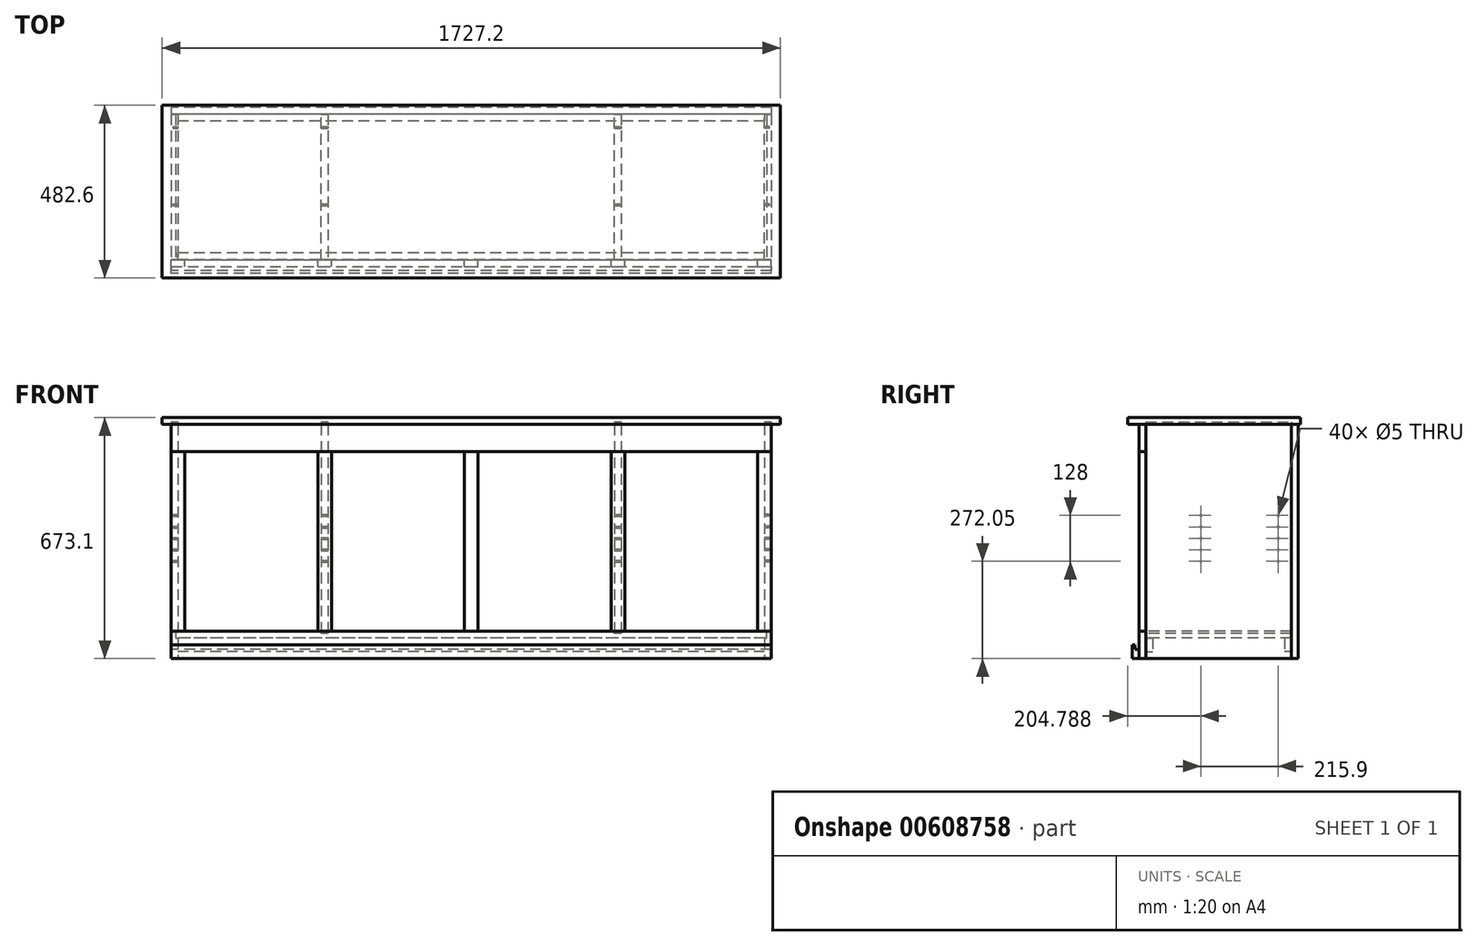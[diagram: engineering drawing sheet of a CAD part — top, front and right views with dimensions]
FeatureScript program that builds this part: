
annotation { "Feature Type Name" : "Feature", "Feature Type Description" : "" }
export const myFeature = defineFeature(function(context is Context, id is Id, definition is map)
    precondition{}
    {
        {
            var Q0;
            Q0=qCreatedBy(makeId("Front.planeOp"),FACE);
            var sketch = newSketch(context, id + "F0", { "sketchPlane" : qUnion([Q0])});
            skLineSegment(sketch, "E0.bottom", {"start": v(838.2, -336.55) * mm, "end": v(-838.2, -336.55) * mm});
            skLineSegment(sketch, "E0.top", {"start": v(838.2, 336.55) * mm, "end": v(-838.2, 336.55) * mm});
            skLineSegment(sketch, "E0.left", {"start": v(838.2, -336.55) * mm, "end": v(838.2, 336.55) * mm});
            skLineSegment(sketch, "E0.right", {"start": v(-838.2, -336.55) * mm, "end": v(-838.2, 336.55) * mm});
            skPoint(sketch, "E0.middle", {"position": v(0, 0) * mm});
            skLineSegment(sketch, "E1", {"start": v(-838.2, 317.5) * mm, "end": v(838.2, 317.5) * mm});
            skLineSegment(sketch, "E2", {"start": v(-838.2, -298.45) * mm, "end": v(838.2, -298.45) * mm});
            skLineSegment(sketch, "E3", {"start": v(-838.2, -260.35) * mm, "end": v(838.2, -260.35) * mm});
            skLineSegment(sketch, "E4", {"start": v(-838.2, 241.3) * mm, "end": v(838.2, 241.3) * mm});
            skLineSegment(sketch, "E5", {"start": v(-800.1, 241.3) * mm, "end": v(-800.1, -260.35) * mm});
            skLineSegment(sketch, "E6", {"start": v(800.1, 241.3) * mm, "end": v(800.1, -260.35) * mm});
            skLineSegment(sketch, "E7", {"start": v(-428.63, 241.3) * mm, "end": v(-428.62, -260.35) * mm});
            skLineSegment(sketch, "E8", {"start": v(-390.53, 241.3) * mm, "end": v(-390.52, -260.35) * mm});
            skLineSegment(sketch, "E9", {"start": v(428.63, 241.3) * mm, "end": v(428.63, -260.35) * mm});
            skLineSegment(sketch, "E10", {"start": v(390.53, 241.3) * mm, "end": v(390.53, -260.35) * mm});
            skLineSegment(sketch, "E11", {"start": v(-19.05, 241.3) * mm, "end": v(-19.05, -260.35) * mm});
            skLineSegment(sketch, "E12", {"start": v(19.05, 241.3) * mm, "end": v(19.05, -260.35) * mm});
            skLineSegment(sketch, "E13", {"start": v(-800.1, -9.53) * mm, "end": v(-428.62, -9.53) * mm, "construction": true});
            skLineSegment(sketch, "E14", {"start": v(-390.52, -9.53) * mm, "end": v(-19.05, -9.52) * mm, "construction": true});
            skLineSegment(sketch, "E15", {"start": v(19.05, -9.52) * mm, "end": v(390.53, -9.52) * mm, "construction": true});
            skLineSegment(sketch, "E16", {"start": v(428.63, -9.52) * mm, "end": v(800.1, -9.52) * mm, "construction": true});
            skLineSegment(sketch, "E17", {"start": v(819.15, 317.5) * mm, "end": v(819.15, -336.55) * mm});
            skLineSegment(sketch, "E18", {"start": v(-819.15, 317.5) * mm, "end": v(-819.15, -336.55) * mm});
            skLineSegment(sketch, "E19", {"start": v(-838.2, -279.4) * mm, "end": v(838.2, -279.4) * mm});
            skLineSegment(sketch, "E20", {"start": v(-419.1, 317.5) * mm, "end": v(-419.1, -260.35) * mm});
            skLineSegment(sketch, "E21", {"start": v(-400.05, 317.5) * mm, "end": v(-400.05, -260.35) * mm});
            skLineSegment(sketch, "E22", {"start": v(400.05, 317.5) * mm, "end": v(400.05, -260.35) * mm});
            skLineSegment(sketch, "E23", {"start": v(419.1, 317.5) * mm, "end": v(419.1, -260.35) * mm});
            skLineSegment(sketch, "E24", {"start": v(-400.05, -260.35) * mm, "end": v(-400.05, -266.7) * mm});
            skLineSegment(sketch, "E25", {"start": v(-400.05, -266.7) * mm, "end": v(-419.1, -266.7) * mm});
            skLineSegment(sketch, "E26", {"start": v(-419.1, -266.7) * mm, "end": v(-419.1, -260.35) * mm});
            skLineSegment(sketch, "E27", {"start": v(400.05, -260.35) * mm, "end": v(400.05, -266.7) * mm});
            skLineSegment(sketch, "E28", {"start": v(419.1, -260.35) * mm, "end": v(419.1, -266.7) * mm});
            skLineSegment(sketch, "E29", {"start": v(419.1, -266.7) * mm, "end": v(400.05, -266.7) * mm});
            skLineSegment(sketch, "E30", {"start": v(825.5, -260.35) * mm, "end": v(825.5, -279.4) * mm});
            skLineSegment(sketch, "E31", {"start": v(-825.5, -260.35) * mm, "end": v(-825.5, -279.4) * mm});
            skLineSegment(sketch, "E32", {"start": v(-838.2, 336.55) * mm, "end": v(-863.6, 336.55) * mm});
            skLineSegment(sketch, "E33", {"start": v(-838.2, 317.5) * mm, "end": v(-863.6, 317.5) * mm});
            skLineSegment(sketch, "E34", {"start": v(-863.6, 336.55) * mm, "end": v(-863.6, 317.5) * mm});
            skLineSegment(sketch, "E35", {"start": v(838.2, 336.55) * mm, "end": v(863.6, 336.55) * mm});
            skLineSegment(sketch, "E36", {"start": v(838.2, 317.5) * mm, "end": v(863.6, 317.5) * mm});
            skLineSegment(sketch, "E37", {"start": v(863.6, 317.5) * mm, "end": v(863.6, 336.55) * mm});
            skLineSegment(sketch, "E38", {"start": v(819.15, 317.5) * mm, "end": v(819.15, 323.85) * mm});
            skLineSegment(sketch, "E39", {"start": v(819.15, 323.85) * mm, "end": v(838.2, 323.85) * mm});
            skLineSegment(sketch, "E40", {"start": v(400.05, 317.5) * mm, "end": v(400.05, 323.85) * mm});
            skLineSegment(sketch, "E41", {"start": v(400.05, 323.85) * mm, "end": v(419.1, 323.85) * mm});
            skLineSegment(sketch, "E42", {"start": v(419.1, 323.85) * mm, "end": v(419.1, 317.5) * mm});
            skLineSegment(sketch, "E43", {"start": v(-419.1, 317.5) * mm, "end": v(-419.1, 323.85) * mm});
            skLineSegment(sketch, "E44", {"start": v(-419.1, 323.85) * mm, "end": v(-400.05, 323.85) * mm});
            skLineSegment(sketch, "E45", {"start": v(-400.05, 323.85) * mm, "end": v(-400.05, 317.5) * mm});
            skLineSegment(sketch, "E46", {"start": v(-819.15, 317.5) * mm, "end": v(-819.15, 323.85) * mm});
            skLineSegment(sketch, "E47", {"start": v(-819.15, 323.85) * mm, "end": v(-838.2, 323.85) * mm});
            skSolve(sketch);
        }
        {
            var Q0;
            Q0=qCreatedBy(makeId("Right.planeOp"),FACE);
            var sketch = newSketch(context, id + "F1", { "sketchPlane" : qUnion([Q0])});
            skSolve(sketch);
        }
        {
            var Q0;
            Q0 = qSketchRegion(id + "F1", true);
            var Q1;
            {var subQ4=sQuery(id+"F0.wireOp",EDGE,"E1");Q1=makeQuery(id+"F0.imprint","IMPRINT",FACE,{"disambiguationData":[TD([[makeQuery(id+"F0.imprint","IMPRINT",EDGE,{"derivedFrom":subQ4}),-1.0]])]});}
            var Q2;
            {var subQ2=sQuery(id+"F0.wireOp",EDGE,"E17");var subQ6=sQuery(id+"F0.wireOp",EDGE,"E1");var subQ7=makeQuery(id+"F0.imprint","INTERSECT",VERTEX,{"derivedFrom":[subQ6,subQ2]});Q2=makeQuery(id+"F0.imprint","IMPRINT",FACE,{"disambiguationData":[TD([[makeQuery(id+"F0.imprint","IMPRINT",EDGE,{"disambiguationData":[TD([[subQ7,1.0]])],"derivedFrom":subQ6}),-1.0]])]});}
            var Q3;
            {var subQ4=sQuery(id+"F0.wireOp",EDGE,"E1");var subQ7=sQuery(id+"F0.wireOp",EDGE,"E18");var subQ9=makeQuery(id+"F0.imprint","INTERSECT",VERTEX,{"derivedFrom":[subQ4,subQ7]});Q3=makeQuery(id+"F0.imprint","IMPRINT",FACE,{"disambiguationData":[TD([[makeQuery(id+"F0.imprint","IMPRINT",EDGE,{"disambiguationData":[TD([[subQ9,-1.0]])],"derivedFrom":subQ4}),-1.0]])]});}
            var Q4;
            {var subQ4=sQuery(id+"F0.wireOp",EDGE,"E1");var subQ8=sQuery(id+"F0.wireOp",EDGE,"E21");var subQ10=makeQuery(id+"F0.imprint","INTERSECT",VERTEX,{"derivedFrom":[subQ4,subQ8]});Q4=makeQuery(id+"F0.imprint","IMPRINT",FACE,{"disambiguationData":[TD([[makeQuery(id+"F0.imprint","IMPRINT",EDGE,{"disambiguationData":[TD([[subQ10,-1.0]])],"derivedFrom":subQ4}),-1.0]])]});}
            extrude(context, id + "F2", {"entities" : qUnion([Q0, Q1, Q2, Q3, Q4]), "depth" : 19.05 * mm, "offsetDistance" : 25.4 * mm});
        }
        {
            var Q0;
            {var subQ0=sQuery(id+"F0.wireOp",EDGE,"E18");var subQ1=sQuery(id+"F0.wireOp",EDGE,"E2");var subQ2=makeQuery(id+"F0.imprint","INTERSECT",VERTEX,{"derivedFrom":[subQ1,subQ0]});Q0=makeQuery(id+"F0.imprint","IMPRINT",FACE,{"disambiguationData":[TD([[makeQuery(id+"F0.imprint","IMPRINT",EDGE,{"disambiguationData":[TD([[subQ2,-1.0]])],"derivedFrom":subQ1}),1.0]])]});}
            var Q1;
            {var subQ0=sQuery(id+"F0.wireOp",EDGE,"E0.left");var subQ1=sQuery(id+"F0.wireOp",EDGE,"E0.bottom");var subQ2=makeQuery(id+"F0.imprint","INTERSECT",VERTEX,{"derivedFrom":[subQ1,subQ0]});Q1=makeQuery(id+"F0.imprint","IMPRINT",FACE,{"disambiguationData":[TD([[makeQuery(id+"F0.imprint","IMPRINT",EDGE,{"disambiguationData":[TD([[subQ2,-1.0]])],"derivedFrom":subQ1}),-1.0]])]});}
            var Q2;
            {var subQ0=sQuery(id+"F0.wireOp",EDGE,"E0.right");var subQ1=sQuery(id+"F0.wireOp",EDGE,"E0.bottom");var subQ2=makeQuery(id+"F0.imprint","INTERSECT",VERTEX,{"derivedFrom":[subQ1,subQ0]});Q2=makeQuery(id+"F0.imprint","IMPRINT",FACE,{"disambiguationData":[TD([[makeQuery(id+"F0.imprint","IMPRINT",EDGE,{"disambiguationData":[TD([[subQ2,1.0]])],"derivedFrom":subQ1}),-1.0]])]});}
            var Q3;
            {var subQ0=sQuery(id+"F0.wireOp",EDGE,"E17");var subQ1=sQuery(id+"F0.wireOp",EDGE,"E0.bottom");var subQ2=makeQuery(id+"F0.imprint","INTERSECT",VERTEX,{"derivedFrom":[subQ1,subQ0]});Q3=makeQuery(id+"F0.imprint","IMPRINT",FACE,{"disambiguationData":[TD([[makeQuery(id+"F0.imprint","IMPRINT",EDGE,{"disambiguationData":[TD([[subQ2,-1.0]])],"derivedFrom":subQ1}),-1.0]])]});}
            var Q4;
            {var subQ5=sQuery(id+"F0.wireOp",EDGE,"E31");Q4=makeQuery(id+"F0.imprint","IMPRINT",FACE,{"disambiguationData":[TD([[makeQuery(id+"F0.imprint","IMPRINT",EDGE,{"derivedFrom":subQ5}),-1.0]])]});}
            var Q5;
            {var subQ14=sQuery(id+"F0.wireOp",EDGE,"E24");Q5=makeQuery(id+"F0.imprint","IMPRINT",FACE,{"disambiguationData":[TD([[makeQuery(id+"F0.imprint","IMPRINT",EDGE,{"derivedFrom":subQ14}),1.0]])]});}
            var Q6;
            {var subQ5=sQuery(id+"F0.wireOp",EDGE,"E30");Q6=makeQuery(id+"F0.imprint","IMPRINT",FACE,{"disambiguationData":[TD([[makeQuery(id+"F0.imprint","IMPRINT",EDGE,{"derivedFrom":subQ5}),1.0]])]});}
            var Q7;
            {var subQ0=sQuery(id+"F0.wireOp",EDGE,"E31");Q7=makeQuery(id+"F0.imprint","IMPRINT",FACE,{"disambiguationData":[TD([[makeQuery(id+"F0.imprint","IMPRINT",EDGE,{"derivedFrom":subQ0}),1.0]])]});}
            var Q8;
            {var subQ1=sQuery(id+"F0.wireOp",EDGE,"E2");var subQ5=sQuery(id+"F0.wireOp",EDGE,"E0.right");var subQ6=makeQuery(id+"F0.imprint","INTERSECT",VERTEX,{"derivedFrom":[subQ5,subQ1]});Q8=makeQuery(id+"F0.imprint","IMPRINT",FACE,{"disambiguationData":[TD([[makeQuery(id+"F0.imprint","IMPRINT",EDGE,{"disambiguationData":[TD([[subQ6,-1.0]])],"derivedFrom":subQ5}),-1.0]])]});}
            var Q9;
            {var subQ2=sQuery(id+"F0.wireOp",EDGE,"E24");Q9=makeQuery(id+"F0.imprint","IMPRINT",FACE,{"disambiguationData":[TD([[makeQuery(id+"F0.imprint","IMPRINT",EDGE,{"derivedFrom":subQ2}),-1.0]])]});}
            var Q10;
            {var subQ0=sQuery(id+"F0.wireOp",EDGE,"E27");Q10=makeQuery(id+"F0.imprint","IMPRINT",FACE,{"disambiguationData":[TD([[makeQuery(id+"F0.imprint","IMPRINT",EDGE,{"derivedFrom":subQ0}),1.0]])]});}
            var Q11;
            {var subQ4=sQuery(id+"F0.wireOp",EDGE,"E2");var subQ6=sQuery(id+"F0.wireOp",EDGE,"E0.left");var subQ7=makeQuery(id+"F0.imprint","INTERSECT",VERTEX,{"derivedFrom":[subQ6,subQ4]});Q11=makeQuery(id+"F0.imprint","IMPRINT",FACE,{"disambiguationData":[TD([[makeQuery(id+"F0.imprint","IMPRINT",EDGE,{"disambiguationData":[TD([[subQ7,-1.0]])],"derivedFrom":subQ6}),1.0]])]});}
            var Q12;
            {var subQ0=sQuery(id+"F0.wireOp",EDGE,"E30");Q12=makeQuery(id+"F0.imprint","IMPRINT",FACE,{"disambiguationData":[TD([[makeQuery(id+"F0.imprint","IMPRINT",EDGE,{"derivedFrom":subQ0}),-1.0]])]});}
            extrude(context, id + "F3", {"entities" : qUnion([Q0, Q1, Q2, Q3, Q4, Q5, Q6, Q7, Q8, Q9, Q10, Q11, Q12]), "depth" : 19.05 * mm, "offsetDistance" : 25.4 * mm});
        }
        {
            var Q0;
            {var subQ5=sQuery(id+"F0.wireOp",EDGE,"E5");Q0=makeQuery(id+"F0.imprint","IMPRINT",FACE,{"disambiguationData":[TD([[makeQuery(id+"F0.imprint","IMPRINT",EDGE,{"derivedFrom":subQ5}),-1.0]])]});}
            var Q1;
            {var subQ0=sQuery(id+"F0.wireOp",EDGE,"E3");var subQ1=sQuery(id+"F0.wireOp",EDGE,"E0.right");var subQ2=makeQuery(id+"F0.imprint","INTERSECT",VERTEX,{"derivedFrom":[subQ1,subQ0]});Q1=makeQuery(id+"F0.imprint","IMPRINT",FACE,{"disambiguationData":[TD([[makeQuery(id+"F0.imprint","IMPRINT",EDGE,{"disambiguationData":[TD([[subQ2,-1.0]])],"derivedFrom":subQ1}),-1.0]])]});}
            extrude(context, id + "F4", {"entities" : qUnion([Q0, Q1]), "depth" : 19.05 * mm, "offsetDistance" : 25.4 * mm});
        }
        {
            var Q0;
            {var subQ0=sQuery(id+"F0.wireOp",EDGE,"E7");Q0=makeQuery(id+"F0.imprint","IMPRINT",FACE,{"disambiguationData":[TD([[makeQuery(id+"F0.imprint","IMPRINT",EDGE,{"derivedFrom":subQ0}),1.0]])]});}
            var Q1;
            {var subQ0=sQuery(id+"F0.wireOp",EDGE,"E20");var subQ1=sQuery(id+"F0.wireOp",EDGE,"E3");var subQ2=makeQuery(id+"F0.imprint","INTERSECT",VERTEX,{"derivedFrom":[subQ1,subQ0]});Q1=makeQuery(id+"F0.imprint","IMPRINT",FACE,{"disambiguationData":[TD([[makeQuery(id+"F0.imprint","IMPRINT",EDGE,{"disambiguationData":[TD([[subQ2,-1.0]])],"derivedFrom":subQ1}),1.0]])]});}
            var Q2;
            {var subQ0=sQuery(id+"F0.wireOp",EDGE,"E8");Q2=makeQuery(id+"F0.imprint","IMPRINT",FACE,{"disambiguationData":[TD([[makeQuery(id+"F0.imprint","IMPRINT",EDGE,{"derivedFrom":subQ0}),-1.0]])]});}
            extrude(context, id + "F5", {"entities" : qUnion([Q0, Q1, Q2]), "depth" : 19.05 * mm, "offsetDistance" : 25.4 * mm});
        }
        {
            var Q0;
            {var subQ0=sQuery(id+"F0.wireOp",EDGE,"E11");Q0=makeQuery(id+"F0.imprint","IMPRINT",FACE,{"disambiguationData":[TD([[makeQuery(id+"F0.imprint","IMPRINT",EDGE,{"derivedFrom":subQ0}),1.0]])]});}
            extrude(context, id + "F6", {"entities" : qUnion([Q0]), "depth" : 19.05 * mm, "offsetDistance" : 25.4 * mm});
        }
        {
            var Q0;
            {var subQ0=sQuery(id+"F0.wireOp",EDGE,"E9");Q0=makeQuery(id+"F0.imprint","IMPRINT",FACE,{"disambiguationData":[TD([[makeQuery(id+"F0.imprint","IMPRINT",EDGE,{"derivedFrom":subQ0}),-1.0]])]});}
            var Q1;
            {var subQ0=sQuery(id+"F0.wireOp",EDGE,"E22");var subQ1=sQuery(id+"F0.wireOp",EDGE,"E3");var subQ2=makeQuery(id+"F0.imprint","INTERSECT",VERTEX,{"derivedFrom":[subQ1,subQ0]});Q1=makeQuery(id+"F0.imprint","IMPRINT",FACE,{"disambiguationData":[TD([[makeQuery(id+"F0.imprint","IMPRINT",EDGE,{"disambiguationData":[TD([[subQ2,-1.0]])],"derivedFrom":subQ1}),1.0]])]});}
            var Q2;
            {var subQ0=sQuery(id+"F0.wireOp",EDGE,"E10");Q2=makeQuery(id+"F0.imprint","IMPRINT",FACE,{"disambiguationData":[TD([[makeQuery(id+"F0.imprint","IMPRINT",EDGE,{"derivedFrom":subQ0}),1.0]])]});}
            extrude(context, id + "F7", {"entities" : qUnion([Q0, Q1, Q2]), "depth" : 19.05 * mm, "offsetDistance" : 25.4 * mm});
        }
        {
            var Q0;
            {var subQ5=sQuery(id+"F0.wireOp",EDGE,"E6");Q0=makeQuery(id+"F0.imprint","IMPRINT",FACE,{"disambiguationData":[TD([[makeQuery(id+"F0.imprint","IMPRINT",EDGE,{"derivedFrom":subQ5}),1.0]])]});}
            var Q1;
            {var subQ0=sQuery(id+"F0.wireOp",EDGE,"E3");var subQ1=sQuery(id+"F0.wireOp",EDGE,"E0.left");var subQ2=makeQuery(id+"F0.imprint","INTERSECT",VERTEX,{"derivedFrom":[subQ1,subQ0]});Q1=makeQuery(id+"F0.imprint","IMPRINT",FACE,{"disambiguationData":[TD([[makeQuery(id+"F0.imprint","IMPRINT",EDGE,{"disambiguationData":[TD([[subQ2,-1.0]])],"derivedFrom":subQ1}),1.0]])]});}
            extrude(context, id + "F8", {"entities" : qUnion([Q0, Q1]), "depth" : 19.05 * mm, "offsetDistance" : 25.4 * mm});
        }
        {
            var Q0;
            Q0=qCreatedBy(makeId("Front.planeOp"),FACE);
            cPlane(context, id + "F9", {"entities" : qUnion([Q0]), "cplaneType" : CPlaneType.OFFSET, "offset" : 406.4 * mm, "oppositeDirection" : true, "width" : 152.4 * mm, "height" : 152.4 * mm});
        }
        {
            var Q0;
            {var subQ0=sQuery(id+"F0.wireOp",EDGE,"E0.top");Q0=makeQuery(id+"F0.imprint","IMPRINT",FACE,{"disambiguationData":[TD([[makeQuery(id+"F0.imprint","IMPRINT",EDGE,{"derivedFrom":subQ0}),1.0]])]});}
            var Q1;
            {var subQ4=sQuery(id+"F0.wireOp",EDGE,"E38");Q1=makeQuery(id+"F0.imprint","IMPRINT",FACE,{"disambiguationData":[TD([[makeQuery(id+"F0.imprint","IMPRINT",EDGE,{"derivedFrom":subQ4}),-1.0]])]});}
            var Q2;
            {var subQ0=sQuery(id+"F0.wireOp",EDGE,"E40");Q2=makeQuery(id+"F0.imprint","IMPRINT",FACE,{"disambiguationData":[TD([[makeQuery(id+"F0.imprint","IMPRINT",EDGE,{"derivedFrom":subQ0}),-1.0]])]});}
            var Q3;
            {var subQ0=sQuery(id+"F0.wireOp",EDGE,"E43");Q3=makeQuery(id+"F0.imprint","IMPRINT",FACE,{"disambiguationData":[TD([[makeQuery(id+"F0.imprint","IMPRINT",EDGE,{"derivedFrom":subQ0}),-1.0]])]});}
            var Q4;
            {var subQ4=sQuery(id+"F0.wireOp",EDGE,"E46");Q4=makeQuery(id+"F0.imprint","IMPRINT",FACE,{"disambiguationData":[TD([[makeQuery(id+"F0.imprint","IMPRINT",EDGE,{"derivedFrom":subQ4}),1.0]])]});}
            var Q5;
            {var subQ1=sQuery(id+"F0.wireOp",EDGE,"E32");Q5=makeQuery(id+"F0.imprint","IMPRINT",FACE,{"disambiguationData":[TD([[makeQuery(id+"F0.imprint","IMPRINT",EDGE,{"derivedFrom":subQ1}),1.0]])]});}
            var Q6;
            {var subQ1=sQuery(id+"F0.wireOp",EDGE,"E35");Q6=makeQuery(id+"F0.imprint","IMPRINT",FACE,{"disambiguationData":[TD([[makeQuery(id+"F0.imprint","IMPRINT",EDGE,{"derivedFrom":subQ1}),-1.0]])]});}
            extrude(context, id + "F10", {"entities" : qUnion([Q0, Q1, Q2, Q3, Q4, Q5, Q6]), "depth" : 50.8 * mm, "offsetDistance" : 25.4 * mm, "hasSecondDirection" : true, "secondDirectionOppositeDirection" : true, "secondDirectionDepth" : 431.8 * mm});
        }
        {
            var Q0;
            {var subQ1=sQuery(id+"F0.wireOp",EDGE,"E3");var subQ10=makeQuery(id+"F0.imprint","INTERSECT",VERTEX,{"derivedFrom":[subQ1,sQuery(id+"F0.wireOp",EDGE,"E5")]});Q0=makeQuery(id+"F0.imprint","IMPRINT",FACE,{"disambiguationData":[TD([[makeQuery(id+"F0.imprint","IMPRINT",EDGE,{"disambiguationData":[TD([[subQ10,1.0]])],"derivedFrom":subQ1}),-1.0]])]});}
            var Q1;
            {var subQ0=sQuery(id+"F0.wireOp",EDGE,"E31");Q1=makeQuery(id+"F0.imprint","IMPRINT",FACE,{"disambiguationData":[TD([[makeQuery(id+"F0.imprint","IMPRINT",EDGE,{"derivedFrom":subQ0}),1.0]])]});}
            var Q2;
            {var subQ0=sQuery(id+"F0.wireOp",EDGE,"E30");Q2=makeQuery(id+"F0.imprint","IMPRINT",FACE,{"disambiguationData":[TD([[makeQuery(id+"F0.imprint","IMPRINT",EDGE,{"derivedFrom":subQ0}),-1.0]])]});}
            var Q3;
            Q3=qCreatedBy(id+"F9.planeOp",FACE);
            extrude(context, id + "F11", {"entities" : qUnion([Q0, Q1, Q2]), "endBound" : BoundingType.UP_TO_SURFACE, "oppositeDirection" : true, "depth" : 25.4 * mm, "endBoundEntityFace" : qUnion([Q3]), "offsetDistance" : 25.4 * mm});
        }
        {
            var Q0;
            {var subQ0=sQuery(id+"F0.wireOp",EDGE,"E3");var subQ1=sQuery(id+"F0.wireOp",EDGE,"E0.left");var subQ2=makeQuery(id+"F0.imprint","INTERSECT",VERTEX,{"derivedFrom":[subQ1,subQ0]});Q0=makeQuery(id+"F0.imprint","IMPRINT",FACE,{"disambiguationData":[TD([[makeQuery(id+"F0.imprint","IMPRINT",EDGE,{"disambiguationData":[TD([[subQ2,-1.0]])],"derivedFrom":subQ1}),1.0]])]});}
            var Q1;
            {var subQ0=sQuery(id+"F0.wireOp",EDGE,"E1");var subQ1=sQuery(id+"F0.wireOp",EDGE,"E0.left");var subQ2=makeQuery(id+"F0.imprint","INTERSECT",VERTEX,{"derivedFrom":[subQ1,subQ0]});Q1=makeQuery(id+"F0.imprint","IMPRINT",FACE,{"disambiguationData":[TD([[makeQuery(id+"F0.imprint","IMPRINT",EDGE,{"disambiguationData":[TD([[subQ2,1.0]])],"derivedFrom":subQ1}),1.0]])]});}
            var Q2;
            {var subQ0=sQuery(id+"F0.wireOp",EDGE,"E3");var subQ1=sQuery(id+"F0.wireOp",EDGE,"E0.left");var subQ2=makeQuery(id+"F0.imprint","INTERSECT",VERTEX,{"derivedFrom":[subQ1,subQ0]});Q2=makeQuery(id+"F0.imprint","IMPRINT",FACE,{"disambiguationData":[TD([[makeQuery(id+"F0.imprint","IMPRINT",EDGE,{"disambiguationData":[TD([[subQ2,1.0]])],"derivedFrom":subQ1}),1.0]])]});}
            var Q3;
            {var subQ0=sQuery(id+"F0.wireOp",EDGE,"E2");var subQ1=sQuery(id+"F0.wireOp",EDGE,"E0.left");var subQ2=makeQuery(id+"F0.imprint","INTERSECT",VERTEX,{"derivedFrom":[subQ1,subQ0]});Q3=makeQuery(id+"F0.imprint","IMPRINT",FACE,{"disambiguationData":[TD([[makeQuery(id+"F0.imprint","IMPRINT",EDGE,{"disambiguationData":[TD([[subQ2,-1.0]])],"derivedFrom":subQ1}),1.0]])]});}
            var Q4;
            {var subQ0=sQuery(id+"F0.wireOp",EDGE,"E0.left");var subQ1=sQuery(id+"F0.wireOp",EDGE,"E0.bottom");var subQ2=makeQuery(id+"F0.imprint","INTERSECT",VERTEX,{"derivedFrom":[subQ1,subQ0]});Q4=makeQuery(id+"F0.imprint","IMPRINT",FACE,{"disambiguationData":[TD([[makeQuery(id+"F0.imprint","IMPRINT",EDGE,{"disambiguationData":[TD([[subQ2,-1.0]])],"derivedFrom":subQ1}),-1.0]])]});}
            var Q5;
            {var subQ4=sQuery(id+"F0.wireOp",EDGE,"E38");Q5=makeQuery(id+"F0.imprint","IMPRINT",FACE,{"disambiguationData":[TD([[makeQuery(id+"F0.imprint","IMPRINT",EDGE,{"derivedFrom":subQ4}),-1.0]])]});}
            var Q6;
            Q6=qCreatedBy(id+"F9.planeOp",FACE);
            extrude(context, id + "F12", {"entities" : qUnion([Q0, Q1, Q2, Q3, Q4, Q5]), "endBound" : BoundingType.UP_TO_SURFACE, "oppositeDirection" : true, "depth" : 25.4 * mm, "endBoundEntityFace" : qUnion([Q6]), "offsetDistance" : 25.4 * mm});
        }
        {
            var Q0;
            {var subQ0=sQuery(id+"F0.wireOp",EDGE,"E3");var subQ1=sQuery(id+"F0.wireOp",EDGE,"E0.right");var subQ2=makeQuery(id+"F0.imprint","INTERSECT",VERTEX,{"derivedFrom":[subQ1,subQ0]});Q0=makeQuery(id+"F0.imprint","IMPRINT",FACE,{"disambiguationData":[TD([[makeQuery(id+"F0.imprint","IMPRINT",EDGE,{"disambiguationData":[TD([[subQ2,-1.0]])],"derivedFrom":subQ1}),-1.0]])]});}
            var Q1;
            {var subQ0=sQuery(id+"F0.wireOp",EDGE,"E1");var subQ1=sQuery(id+"F0.wireOp",EDGE,"E0.right");var subQ2=makeQuery(id+"F0.imprint","INTERSECT",VERTEX,{"derivedFrom":[subQ1,subQ0]});Q1=makeQuery(id+"F0.imprint","IMPRINT",FACE,{"disambiguationData":[TD([[makeQuery(id+"F0.imprint","IMPRINT",EDGE,{"disambiguationData":[TD([[subQ2,1.0]])],"derivedFrom":subQ1}),-1.0]])]});}
            var Q2;
            {var subQ0=sQuery(id+"F0.wireOp",EDGE,"E0.right");var subQ1=sQuery(id+"F0.wireOp",EDGE,"E0.bottom");var subQ2=makeQuery(id+"F0.imprint","INTERSECT",VERTEX,{"derivedFrom":[subQ1,subQ0]});Q2=makeQuery(id+"F0.imprint","IMPRINT",FACE,{"disambiguationData":[TD([[makeQuery(id+"F0.imprint","IMPRINT",EDGE,{"disambiguationData":[TD([[subQ2,1.0]])],"derivedFrom":subQ1}),-1.0]])]});}
            var Q3;
            {var subQ0=sQuery(id+"F0.wireOp",EDGE,"E2");var subQ1=sQuery(id+"F0.wireOp",EDGE,"E0.right");var subQ2=makeQuery(id+"F0.imprint","INTERSECT",VERTEX,{"derivedFrom":[subQ1,subQ0]});Q3=makeQuery(id+"F0.imprint","IMPRINT",FACE,{"disambiguationData":[TD([[makeQuery(id+"F0.imprint","IMPRINT",EDGE,{"disambiguationData":[TD([[subQ2,-1.0]])],"derivedFrom":subQ1}),-1.0]])]});}
            var Q4;
            {var subQ0=sQuery(id+"F0.wireOp",EDGE,"E3");var subQ1=sQuery(id+"F0.wireOp",EDGE,"E0.right");var subQ2=makeQuery(id+"F0.imprint","INTERSECT",VERTEX,{"derivedFrom":[subQ1,subQ0]});Q4=makeQuery(id+"F0.imprint","IMPRINT",FACE,{"disambiguationData":[TD([[makeQuery(id+"F0.imprint","IMPRINT",EDGE,{"disambiguationData":[TD([[subQ2,1.0]])],"derivedFrom":subQ1}),-1.0]])]});}
            var Q5;
            {var subQ4=sQuery(id+"F0.wireOp",EDGE,"E46");Q5=makeQuery(id+"F0.imprint","IMPRINT",FACE,{"disambiguationData":[TD([[makeQuery(id+"F0.imprint","IMPRINT",EDGE,{"derivedFrom":subQ4}),1.0]])]});}
            var Q6;
            Q6=qCreatedBy(id+"F9.planeOp",FACE);
            extrude(context, id + "F13", {"entities" : qUnion([Q0, Q1, Q2, Q3, Q4, Q5]), "endBound" : BoundingType.UP_TO_SURFACE, "oppositeDirection" : true, "depth" : 25.4 * mm, "endBoundEntityFace" : qUnion([Q6]), "offsetDistance" : 25.4 * mm});
        }
        {
            var Q0;
            Q0=qCreatedBy(makeId("Right.planeOp"),FACE);
            var sketch = newSketch(context, id + "F14", { "sketchPlane" : qUnion([Q0])});
            skLineSegment(sketch, "E48.bottom", {"start": v(-19.05, -336.55) * mm, "end": v(-38.1, -336.55) * mm});
            skLineSegment(sketch, "E48.top", {"start": v(-19.05, -298.45) * mm, "end": v(-38.1, -298.45) * mm});
            skLineSegment(sketch, "E48.left", {"start": v(-19.05, -336.55) * mm, "end": v(-19.05, -298.45) * mm});
            skLineSegment(sketch, "E48.right", {"start": v(-38.1, -336.55) * mm, "end": v(-38.1, -298.45) * mm});
            skLineSegment(sketch, "E49", {"start": v(-30.16, -298.45) * mm, "end": v(-30.16, -311.15) * mm});
            skLineSegment(sketch, "E50", {"start": v(-30.16, -311.15) * mm, "end": v(-19.05, -311.15) * mm});
            skLineSegment(sketch, "E51.bottom", {"start": v(0, -279.4) * mm, "end": v(19.05, -279.4) * mm});
            skLineSegment(sketch, "E51.top", {"start": v(0, -317.5) * mm, "end": v(19.05, -317.5) * mm});
            skLineSegment(sketch, "E51.left", {"start": v(0, -279.4) * mm, "end": v(0, -317.5) * mm});
            skLineSegment(sketch, "E51.right", {"start": v(19.05, -279.4) * mm, "end": v(19.05, -317.5) * mm});
            skLineSegment(sketch, "E52.bottom", {"start": v(406.4, -279.4) * mm, "end": v(387.35, -279.4) * mm});
            skLineSegment(sketch, "E52.top", {"start": v(406.4, -317.5) * mm, "end": v(387.35, -317.5) * mm});
            skLineSegment(sketch, "E52.left", {"start": v(406.4, -279.4) * mm, "end": v(406.4, -317.5) * mm});
            skLineSegment(sketch, "E52.right", {"start": v(387.35, -279.4) * mm, "end": v(387.35, -317.5) * mm});
            skSolve(sketch);
        }
        {
            var Q0;
            Q0=makeQuery(id+"F14.imprint","IMPRINT",FACE,{"disambiguationData":[TD([[makeQuery(id+"F14.imprint","IMPRINT",EDGE,{"derivedFrom":sQuery(id+"F14.wireOp",EDGE,"E48.bottom")}),-1.0]])]});
            var Q1;
            Q1=makeQuery(id+"F3.opExtrude","SWEPT_FACE",FACE,{"disambiguationData":[OSD([sQuery(id+"F0.wireOp",EDGE,"E0.left")])]});
            var Q2;
            Q2=makeQuery(id+"F3.opExtrude","SWEPT_FACE",FACE,{"disambiguationData":[OSD([sQuery(id+"F0.wireOp",EDGE,"E0.right")])]});
            extrude(context, id + "F15", {"entities" : qUnion([Q0]), "endBound" : BoundingType.UP_TO_SURFACE, "depth" : 25.4 * mm, "endBoundEntityFace" : qUnion([Q1]), "offsetDistance" : 25.4 * mm, "hasSecondDirection" : true, "secondDirectionBound" : SecondDirectionBoundingType.UP_TO_SURFACE, "secondDirectionOppositeDirection" : true, "secondDirectionDepth" : 25.4 * mm, "secondDirectionBoundEntityFace" : qUnion([Q2])});
        }
        {
            var Q0;
            {var subQ0=sQuery(id+"F0.wireOp",EDGE,"E22");var subQ1=sQuery(id+"F0.wireOp",EDGE,"E1");var subQ2=makeQuery(id+"F0.imprint","INTERSECT",VERTEX,{"derivedFrom":[subQ1,subQ0]});Q0=makeQuery(id+"F0.imprint","IMPRINT",FACE,{"disambiguationData":[TD([[makeQuery(id+"F0.imprint","IMPRINT",EDGE,{"disambiguationData":[TD([[subQ2,-1.0]])],"derivedFrom":subQ1}),-1.0]])]});}
            var Q1;
            {var subQ0=sQuery(id+"F0.wireOp",EDGE,"E22");var subQ1=sQuery(id+"F0.wireOp",EDGE,"E3");var subQ2=makeQuery(id+"F0.imprint","INTERSECT",VERTEX,{"derivedFrom":[subQ1,subQ0]});Q1=makeQuery(id+"F0.imprint","IMPRINT",FACE,{"disambiguationData":[TD([[makeQuery(id+"F0.imprint","IMPRINT",EDGE,{"disambiguationData":[TD([[subQ2,-1.0]])],"derivedFrom":subQ1}),1.0]])]});}
            var Q2;
            {var subQ0=sQuery(id+"F0.wireOp",EDGE,"E40");Q2=makeQuery(id+"F0.imprint","IMPRINT",FACE,{"disambiguationData":[TD([[makeQuery(id+"F0.imprint","IMPRINT",EDGE,{"derivedFrom":subQ0}),-1.0]])]});}
            var Q3;
            {var subQ0=sQuery(id+"F0.wireOp",EDGE,"E27");Q3=makeQuery(id+"F0.imprint","IMPRINT",FACE,{"disambiguationData":[TD([[makeQuery(id+"F0.imprint","IMPRINT",EDGE,{"derivedFrom":subQ0}),1.0]])]});}
            var Q4;
            Q4=qCreatedBy(id+"F9.planeOp",FACE);
            extrude(context, id + "F16", {"entities" : qUnion([Q0, Q1, Q2, Q3]), "endBound" : BoundingType.UP_TO_SURFACE, "oppositeDirection" : true, "depth" : 25.4 * mm, "endBoundEntityFace" : qUnion([Q4]), "offsetDistance" : 25.4 * mm});
        }
        {
            var Q0;
            {var subQ0=sQuery(id+"F0.wireOp",EDGE,"E20");var subQ1=sQuery(id+"F0.wireOp",EDGE,"E1");var subQ2=makeQuery(id+"F0.imprint","INTERSECT",VERTEX,{"derivedFrom":[subQ1,subQ0]});Q0=makeQuery(id+"F0.imprint","IMPRINT",FACE,{"disambiguationData":[TD([[makeQuery(id+"F0.imprint","IMPRINT",EDGE,{"disambiguationData":[TD([[subQ2,-1.0]])],"derivedFrom":subQ1}),-1.0]])]});}
            var Q1;
            {var subQ0=sQuery(id+"F0.wireOp",EDGE,"E20");var subQ1=sQuery(id+"F0.wireOp",EDGE,"E3");var subQ2=makeQuery(id+"F0.imprint","INTERSECT",VERTEX,{"derivedFrom":[subQ1,subQ0]});Q1=makeQuery(id+"F0.imprint","IMPRINT",FACE,{"disambiguationData":[TD([[makeQuery(id+"F0.imprint","IMPRINT",EDGE,{"disambiguationData":[TD([[subQ2,-1.0]])],"derivedFrom":subQ1}),1.0]])]});}
            var Q2;
            {var subQ0=sQuery(id+"F0.wireOp",EDGE,"E43");Q2=makeQuery(id+"F0.imprint","IMPRINT",FACE,{"disambiguationData":[TD([[makeQuery(id+"F0.imprint","IMPRINT",EDGE,{"derivedFrom":subQ0}),-1.0]])]});}
            var Q3;
            {var subQ2=sQuery(id+"F0.wireOp",EDGE,"E24");Q3=makeQuery(id+"F0.imprint","IMPRINT",FACE,{"disambiguationData":[TD([[makeQuery(id+"F0.imprint","IMPRINT",EDGE,{"derivedFrom":subQ2}),-1.0]])]});}
            var Q4;
            Q4=qCreatedBy(id+"F9.planeOp",FACE);
            extrude(context, id + "F17", {"entities" : qUnion([Q0, Q1, Q2, Q3]), "endBound" : BoundingType.UP_TO_SURFACE, "oppositeDirection" : true, "depth" : 25.4 * mm, "endBoundEntityFace" : qUnion([Q4]), "offsetDistance" : 25.4 * mm});
        }
        {
            var Q0;
            Q0=qCreatedBy(id+"F9.planeOp",FACE);
            var sketch = newSketch(context, id + "F18", { "sketchPlane" : qUnion([Q0])});
            skLineSegment(sketch, "E53.0", {"start": v(838.2, 336.55) * mm, "end": v(-838.2, 336.55) * mm});
            skLineSegment(sketch, "E54.0", {"start": v(838.2, -336.55) * mm, "end": v(838.2, 336.55) * mm});
            skLineSegment(sketch, "E55.0", {"start": v(838.2, -336.55) * mm, "end": v(-838.2, -336.55) * mm});
            skLineSegment(sketch, "E56.0", {"start": v(-838.2, -336.55) * mm, "end": v(-838.2, 336.55) * mm});
            skLineSegment(sketch, "E57.0", {"start": v(-838.2, 317.5) * mm, "end": v(838.2, 317.5) * mm});
            skSolve(sketch);
        }
        {
            var Q0;
            {var subQ0=sQuery(id+"F18.wireOp",EDGE,"E55.0");Q0=makeQuery(id+"F18.imprint","IMPRINT",FACE,{"disambiguationData":[TD([[makeQuery(id+"F18.imprint","IMPRINT",EDGE,{"derivedFrom":subQ0}),-1.0]])]});}
            extrude(context, id + "F19", {"entities" : qUnion([Q0]), "oppositeDirection" : true, "depth" : 19.05 * mm, "offsetDistance" : 25.4 * mm});
        }
        {
            var Q0;
            Q0=makeQuery(id+"F12.opExtrude","SWEPT_FACE",FACE,{"disambiguationData":[OSD([sQuery(id+"F0.wireOp",EDGE,"E0.left")])]});
            var sketch = newSketch(context, id + "F20", { "sketchPlane" : qUnion([Q0])});
            skLineSegment(sketch, "E58", {"start": v(369.89, 63.5) * mm, "end": v(153.99, 63.5) * mm, "construction": true});
            skLineSegment(sketch, "E59.0.1.0", {"start": v(369.89, 31.5) * mm, "end": v(153.99, 31.5) * mm, "construction": true});
            skLineSegment(sketch, "E59.0.2.0", {"start": v(369.89, -0.5) * mm, "end": v(153.99, -0.5) * mm, "construction": true});
            skLineSegment(sketch, "E59.0.3.0", {"start": v(369.89, -32.5) * mm, "end": v(153.99, -32.5) * mm, "construction": true});
            skLineSegment(sketch, "E59.0.4.0", {"start": v(369.89, -64.5) * mm, "end": v(153.99, -64.5) * mm, "construction": true});
            skLineSegment(sketch, "E59.direction1", {"start": v(369.89, 63.5) * mm, "end": v(395.29, 63.5) * mm, "construction": true});
            skLineSegment(sketch, "E59.direction2", {"start": v(369.89, 63.5) * mm, "end": v(369.89, 31.5) * mm, "construction": true});
            skSolve(sketch);
        }
        {
            var Q0;
            Q0=sQuery(id+"F20.wireOp",VERTEX,"E59.0.1.0.start");
            var Q1;
            Q1=sQuery(id+"F20.wireOp",VERTEX,"E59.0.3.0.start");
            var Q2;
            Q2=sQuery(id+"F20.wireOp",VERTEX,"E59.0.4.0.start");
            var Q3;
            Q3=sQuery(id+"F20.wireOp",VERTEX,"E59.0.3.0.end");
            var Q4;
            Q4=sQuery(id+"F20.wireOp",VERTEX,"E59.0.4.0.end");
            var Q5;
            Q5=sQuery(id+"F20.wireOp",VERTEX,"E59.0.2.0.end");
            var Q6;
            Q6=sQuery(id+"F20.wireOp",VERTEX,"E59.0.2.0.start");
            var Q7;
            Q7=sQuery(id+"F20.wireOp",VERTEX,"E59.0.1.0.end");
            var Q8;
            Q8=sQuery(id+"F20.wireOp",VERTEX,"E58.end");
            var Q9;
            Q9=sQuery(id+"F20.wireOp",VERTEX,"E59.direction2.start");
            var Q10;
            Q10=makeQuery(id+"F16.opExtrude","SWEPT_BODY",BODY,{"disambiguationData":[OSD([sQuery(id+"F0.wireOp",EDGE,"E1"),sQuery(id+"F0.wireOp",EDGE,"E3"),sQuery(id+"F0.wireOp",EDGE,"E22"),sQuery(id+"F0.wireOp",EDGE,"E23")])]});
            var Q11;
            Q11=makeQuery(id+"F17.opExtrude","SWEPT_BODY",BODY,{"disambiguationData":[OSD([sQuery(id+"F0.wireOp",EDGE,"E1"),sQuery(id+"F0.wireOp",EDGE,"E3"),sQuery(id+"F0.wireOp",EDGE,"E20"),sQuery(id+"F0.wireOp",EDGE,"E21")])]});
            hole(context, id + "F21", {"style" : HoleStyle.SIMPLE, "endStyle" : HoleEndStyle.THROUGH, "standardTappedOrClearance" : lookupTablePath({ "standard" : "ISO", "size" : "5", "type" : "Drilled" }), "standardBlindInLast" : lookupTablePath({ "standard" : "ISO", "size" : "5", "type" : "Drilled" }), "holeDiameter" : 5 * mm, "majorDiameter" : 6.35 * mm, "isTappedThrough" : true, "tappedDepth" : 12.7 * mm, "tapClearance" : 3, "locations" : qUnion([Q0, Q1, Q2, Q3, Q4, Q5, Q6, Q7, Q8, Q9]), "scope" : qUnion([Q10, Q11])});
        }
        {
            var Q0;
            Q0=sQuery(id+"F20.wireOp",VERTEX,"E59.direction2.start");
            var Q1;
            Q1=sQuery(id+"F20.wireOp",VERTEX,"E59.0.1.0.start");
            var Q2;
            Q2=sQuery(id+"F20.wireOp",VERTEX,"E59.0.2.0.start");
            var Q3;
            Q3=sQuery(id+"F20.wireOp",VERTEX,"E59.0.3.0.start");
            var Q4;
            Q4=sQuery(id+"F20.wireOp",VERTEX,"E59.0.4.0.start");
            var Q5;
            Q5=sQuery(id+"F20.wireOp",VERTEX,"E59.0.4.0.end");
            var Q6;
            Q6=sQuery(id+"F20.wireOp",VERTEX,"E59.0.3.0.end");
            var Q7;
            Q7=sQuery(id+"F20.wireOp",VERTEX,"E59.0.2.0.end");
            var Q8;
            Q8=sQuery(id+"F20.wireOp",VERTEX,"E59.0.1.0.end");
            var Q9;
            Q9=sQuery(id+"F20.wireOp",VERTEX,"E58.end");
            var Q10;
            Q10=makeQuery(id+"F13.opExtrude","SWEPT_BODY",BODY,{"disambiguationData":[OSD([sQuery(id+"F0.wireOp",EDGE,"E0.bottom"),sQuery(id+"F0.wireOp",EDGE,"E0.right"),sQuery(id+"F0.wireOp",EDGE,"E1"),sQuery(id+"F0.wireOp",EDGE,"E3"),sQuery(id+"F0.wireOp",EDGE,"E18"),sQuery(id+"F0.wireOp",EDGE,"E19"),sQuery(id+"F0.wireOp",EDGE,"E31")])]});
            hole(context, id + "F22", {"style" : HoleStyle.SIMPLE, "endStyle" : HoleEndStyle.BLIND, "standardTappedOrClearance" : lookupTablePath({ "standard" : "ISO", "size" : "5", "type" : "Drilled" }), "standardBlindInLast" : lookupTablePath({ "standard" : "ISO", "size" : "5", "type" : "Drilled" }), "holeDiameter" : 5 * mm, "majorDiameter" : 6.35 * mm, "holeDepth" : 12.7 * mm, "isTappedThrough" : true, "tappedDepth" : 12.7 * mm, "tapClearance" : 3, "locations" : qUnion([Q0, Q1, Q2, Q3, Q4, Q5, Q6, Q7, Q8, Q9]), "scope" : qUnion([Q10])});
        }
        {
            var Q0;
            {var subQ0=sQuery(id+"F0.wireOp",EDGE,"E17");Q0=makeQuery(id+"F12.opExtrude","SWEPT_FACE",FACE,{"disambiguationData":[OSD([subQ0]),TDD([makeQuery(id+"F0.imprint","IMPRINT",EDGE,{"disambiguationData":[TD([[makeQuery(id+"F0.imprint","INTERSECT",VERTEX,{"derivedFrom":[sQuery(id+"F0.wireOp",EDGE,"E1"),subQ0]}),-1.0]])],"derivedFrom":subQ0}),makeQuery(id+"F0.imprint","IMPRINT",EDGE,{"disambiguationData":[TD([[makeQuery(id+"F0.imprint","INTERSECT",VERTEX,{"derivedFrom":[sQuery(id+"F0.wireOp",EDGE,"E3"),subQ0]}),1.0]])],"derivedFrom":subQ0})])]});}
            var sketch = newSketch(context, id + "F23", { "sketchPlane" : qUnion([Q0])});
            skPoint(sketch, "E60", {"position": v(-369.89, 63.5) * mm});
            skPoint(sketch, "E61", {"position": v(-369.89, 31.5) * mm});
            skPoint(sketch, "E62", {"position": v(-369.89, -0.5) * mm});
            skPoint(sketch, "E63", {"position": v(-369.89, -32.5) * mm});
            skPoint(sketch, "E64", {"position": v(-369.89, -64.5) * mm});
            skPoint(sketch, "E65", {"position": v(-153.99, -64.5) * mm});
            skPoint(sketch, "E66", {"position": v(-153.99, -32.5) * mm});
            skPoint(sketch, "E67", {"position": v(-153.99, -0.5) * mm});
            skPoint(sketch, "E68", {"position": v(-153.99, 31.5) * mm});
            skPoint(sketch, "E69", {"position": v(-153.99, 63.5) * mm});
            skSolve(sketch);
        }
        {
            var Q0;
            Q0=sQuery(id+"F23.wireOp",VERTEX,"E68");
            var Q1;
            Q1=sQuery(id+"F23.wireOp",VERTEX,"E67");
            var Q2;
            Q2=sQuery(id+"F23.wireOp",VERTEX,"E66");
            var Q3;
            Q3=sQuery(id+"F23.wireOp",VERTEX,"E65");
            var Q4;
            Q4=sQuery(id+"F23.wireOp",VERTEX,"E69");
            var Q5;
            Q5=sQuery(id+"F23.wireOp",VERTEX,"E60");
            var Q6;
            Q6=sQuery(id+"F23.wireOp",VERTEX,"E61");
            var Q7;
            Q7=sQuery(id+"F23.wireOp",VERTEX,"E62");
            var Q8;
            Q8=sQuery(id+"F23.wireOp",VERTEX,"E63");
            var Q9;
            Q9=sQuery(id+"F23.wireOp",VERTEX,"E64");
            var Q10;
            Q10=makeQuery(id+"F12.opExtrude","SWEPT_BODY",BODY,{"disambiguationData":[OSD([sQuery(id+"F0.wireOp",EDGE,"E0.bottom"),sQuery(id+"F0.wireOp",EDGE,"E0.left"),sQuery(id+"F0.wireOp",EDGE,"E1"),sQuery(id+"F0.wireOp",EDGE,"E3"),sQuery(id+"F0.wireOp",EDGE,"E17"),sQuery(id+"F0.wireOp",EDGE,"E19"),sQuery(id+"F0.wireOp",EDGE,"E30")])]});
            hole(context, id + "F24", {"style" : HoleStyle.SIMPLE, "endStyle" : HoleEndStyle.BLIND, "standardTappedOrClearance" : lookupTablePath({ "standard" : "ISO", "size" : "5", "type" : "Drilled" }), "standardBlindInLast" : lookupTablePath({ "standard" : "ISO", "size" : "5", "type" : "Drilled" }), "holeDiameter" : 5 * mm, "majorDiameter" : 6.35 * mm, "holeDepth" : 12.7 * mm, "isTappedThrough" : true, "tappedDepth" : 12.7 * mm, "tapClearance" : 3, "startFromSketch" : true, "locations" : qUnion([Q0, Q1, Q2, Q3, Q4, Q5, Q6, Q7, Q8, Q9]), "scope" : qUnion([Q10])});
        }
        {
            var Q0;
            Q0=makeQuery(id+"F10.opExtrude","SWEPT_FACE",FACE,{"disambiguationData":[OSD([sQuery(id+"F0.wireOp",EDGE,"E1"),sQuery(id+"F0.wireOp",EDGE,"E33"),sQuery(id+"F0.wireOp",EDGE,"E36")])]});
            var sketch = newSketch(context, id + "F25", { "sketchPlane" : qUnion([Q0])});
            skLineSegment(sketch, "E70.0.0", {"start": v(-838.2, 0) * mm, "end": v(-838.2, -406.4) * mm});
            skLineSegment(sketch, "E70.0.1", {"start": v(-838.2, -406.4) * mm, "end": v(-819.15, -406.4) * mm});
            skLineSegment(sketch, "E70.0.2", {"start": v(-819.15, -406.4) * mm, "end": v(-819.15, 0) * mm});
            skLineSegment(sketch, "E70.0.3", {"start": v(-819.15, 0) * mm, "end": v(-838.2, 0) * mm});
            skLineSegment(sketch, "E70.1.0", {"start": v(-419.1, 0) * mm, "end": v(-419.1, -406.4) * mm});
            skLineSegment(sketch, "E70.1.1", {"start": v(-419.1, -406.4) * mm, "end": v(-400.05, -406.4) * mm});
            skLineSegment(sketch, "E70.1.2", {"start": v(-400.05, -406.4) * mm, "end": v(-400.05, 0) * mm});
            skLineSegment(sketch, "E70.1.3", {"start": v(-400.05, 0) * mm, "end": v(-419.1, 0) * mm});
            skLineSegment(sketch, "E70.2.0", {"start": v(400.05, 0) * mm, "end": v(400.05, -406.4) * mm});
            skLineSegment(sketch, "E70.2.1", {"start": v(400.05, -406.4) * mm, "end": v(419.1, -406.4) * mm});
            skLineSegment(sketch, "E70.2.2", {"start": v(419.1, -406.4) * mm, "end": v(419.1, 0) * mm});
            skLineSegment(sketch, "E70.2.3", {"start": v(419.1, 0) * mm, "end": v(400.05, 0) * mm});
            skLineSegment(sketch, "E70.3.0", {"start": v(819.15, 0) * mm, "end": v(819.15, -406.4) * mm});
            skLineSegment(sketch, "E70.3.1", {"start": v(819.15, -406.4) * mm, "end": v(838.2, -406.4) * mm});
            skLineSegment(sketch, "E70.3.2", {"start": v(838.2, -406.4) * mm, "end": v(838.2, 0) * mm});
            skLineSegment(sketch, "E70.3.3", {"start": v(838.2, 0) * mm, "end": v(819.15, 0) * mm});
            skSolve(sketch);
        }
        {
            var Q0;
            Q0=makeQuery(id+"F25.imprint","IMPRINT",FACE,{"disambiguationData":[TD([[makeQuery(id+"F25.imprint","IMPRINT",EDGE,{"derivedFrom":sQuery(id+"F25.wireOp",EDGE,"E70.0.0")}),1.0]])]});
            var Q1;
            Q1=makeQuery(id+"F25.imprint","IMPRINT",FACE,{"disambiguationData":[TD([[makeQuery(id+"F25.imprint","IMPRINT",EDGE,{"derivedFrom":sQuery(id+"F25.wireOp",EDGE,"E70.1.0")}),1.0]])]});
            var Q2;
            Q2=makeQuery(id+"F25.imprint","IMPRINT",FACE,{"disambiguationData":[TD([[makeQuery(id+"F25.imprint","IMPRINT",EDGE,{"derivedFrom":sQuery(id+"F25.wireOp",EDGE,"E70.2.0")}),1.0]])]});
            var Q3;
            Q3=makeQuery(id+"F25.imprint","IMPRINT",FACE,{"disambiguationData":[TD([[makeQuery(id+"F25.imprint","IMPRINT",EDGE,{"derivedFrom":sQuery(id+"F25.wireOp",EDGE,"E70.3.0")}),1.0]])]});
            extrude(context, id + "F26", {"entities" : qUnion([Q0, Q1, Q2, Q3]), "operationType" : NewBodyOperationType.REMOVE, "oppositeDirection" : true, "depth" : 6.35 * mm, "offsetDistance" : 25.4 * mm});
        }
        {
            var Q0;
            Q0=makeQuery(id+"F14.imprint","IMPRINT",FACE,{"disambiguationData":[TD([[makeQuery(id+"F14.imprint","IMPRINT",EDGE,{"derivedFrom":sQuery(id+"F14.wireOp",EDGE,"E51.bottom")}),-1.0]])]});
            extrude(context, id + "F27", {"entities" : qUnion([Q0]), "endBound" : BoundingType.SYMMETRIC, "depth" : 1638.3 * mm, "offsetDistance" : 25.4 * mm});
        }
        {
            var Q0;
            Q0=makeQuery(id+"F14.imprint","IMPRINT",FACE,{"disambiguationData":[TD([[makeQuery(id+"F14.imprint","IMPRINT",EDGE,{"derivedFrom":sQuery(id+"F14.wireOp",EDGE,"E52.bottom")}),1.0]])]});
            extrude(context, id + "F28", {"entities" : qUnion([Q0]), "endBound" : BoundingType.SYMMETRIC, "depth" : 1638.3 * mm, "offsetDistance" : 25.4 * mm});
        }
    });
